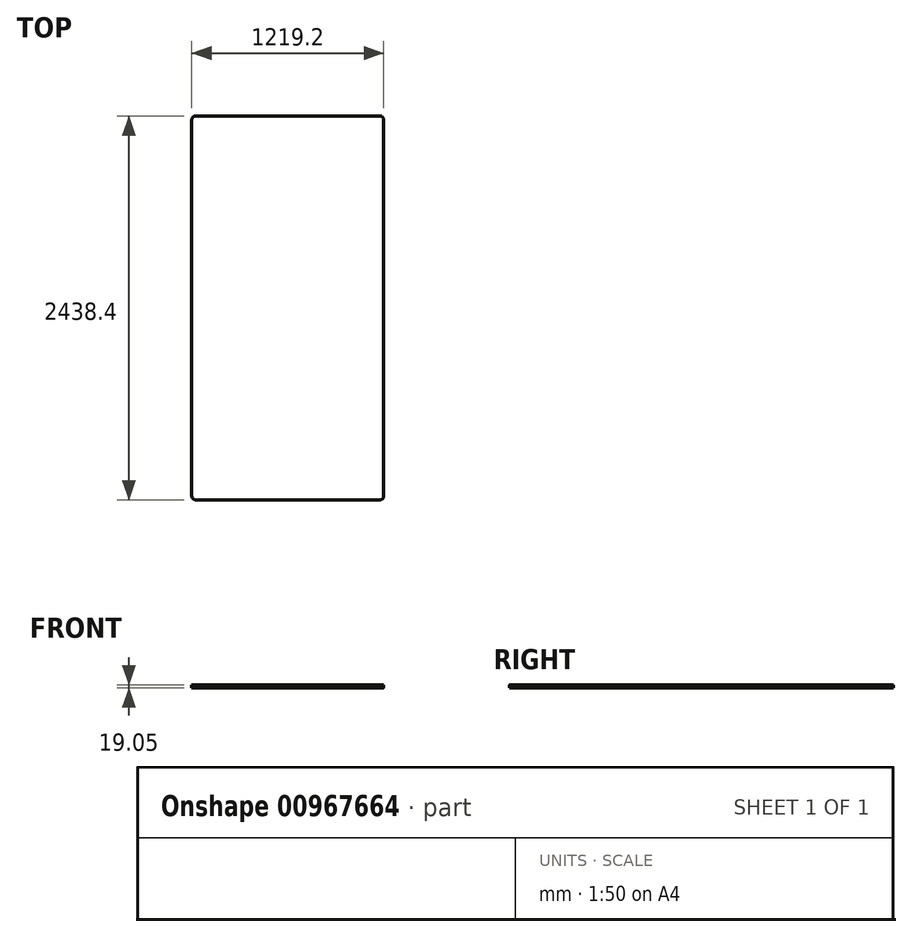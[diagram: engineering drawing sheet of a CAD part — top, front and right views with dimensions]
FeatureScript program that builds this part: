
annotation { "Feature Type Name" : "Feature", "Feature Type Description" : "" }
export const myFeature = defineFeature(function(context is Context, id is Id, definition is map)
    precondition{}
    {
        {
            var Q0;
            Q0=qCreatedBy(makeId("Top.planeOp"),FACE);
            var sketch = newSketch(context, id + "F0", { "sketchPlane" : qUnion([Q0])});
            skLineSegment(sketch, "E0.bottom", {"start": v(25.4, 0) * mm, "end": v(1193.8, 0) * mm});
            skLineSegment(sketch, "E0.top", {"start": v(25.4, 2438.4) * mm, "end": v(1193.8, 2438.4) * mm});
            skLineSegment(sketch, "E0.left", {"start": v(0, 25.4) * mm, "end": v(0, 2413) * mm});
            skLineSegment(sketch, "E0.right", {"start": v(1219.2, 25.4) * mm, "end": v(1219.2, 2413) * mm});
            skPoint(sketch, "E1.visualSharp", {"position": v(0, 0) * mm});
            skArc(sketch, "E1.filletArc", {"start": v(0, 25.4) * mm, "mid": v(7.44, 7.44) * mm, "end": v(25.4, 0) * mm});
            skPoint(sketch, "E2.visualSharp", {"position": v(1219.2, 0) * mm});
            skArc(sketch, "E2.filletArc", {"start": v(1193.8, 0) * mm, "mid": v(1211.76, 7.44) * mm, "end": v(1219.2, 25.4) * mm});
            skPoint(sketch, "E3.visualSharp", {"position": v(1219.2, 2438.4) * mm});
            skArc(sketch, "E3.filletArc", {"start": v(1219.2, 2413) * mm, "mid": v(1211.76, 2430.96) * mm, "end": v(1193.8, 2438.4) * mm});
            skPoint(sketch, "E4.visualSharp", {"position": v(0, 2438.4) * mm});
            skArc(sketch, "E4.filletArc", {"start": v(25.4, 2438.4) * mm, "mid": v(7.44, 2430.96) * mm, "end": v(0, 2413) * mm});
            skSolve(sketch);
        }
        {
            var Q0;
            Q0 = qSketchRegion(id + "F0", true);
            extrude(context, id + "F1", {"entities" : qUnion([Q0]), "depth" : 19.05 * mm, "offsetDistance" : 25.4 * mm});
        }
    });
